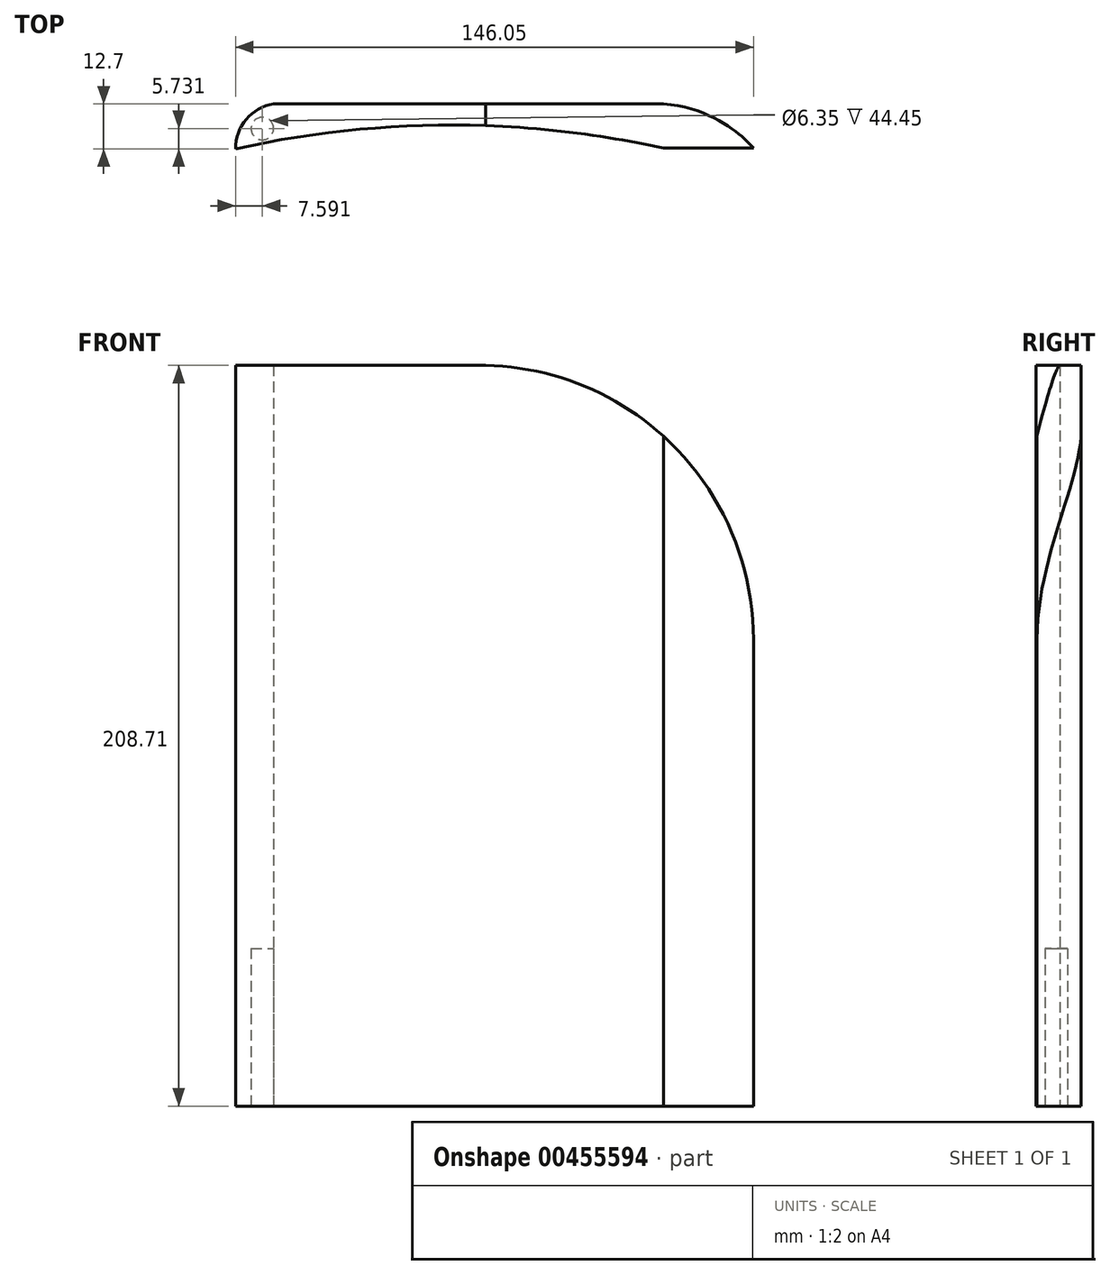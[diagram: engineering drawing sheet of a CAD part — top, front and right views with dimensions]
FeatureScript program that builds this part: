
annotation { "Feature Type Name" : "Feature", "Feature Type Description" : "" }
export const myFeature = defineFeature(function(context is Context, id is Id, definition is map)
    precondition{}
    {
        {
            var Q0;
            Q0=qCreatedBy(makeId("Front.planeOp"),FACE);
            var sketch = newSketch(context, id + "F0", { "sketchPlane" : qUnion([Q0])});
            skLineSegment(sketch, "E0", {"start": v(0, 0) * mm, "end": v(146.05, 0) * mm});
            skLineSegment(sketch, "E1", {"start": v(146.05, 0) * mm, "end": v(146.05, 131.57) * mm});
            skLineSegment(sketch, "E2", {"start": v(146.05, 131.57) * mm, "end": v(70.54, 208.71) * mm});
            skLineSegment(sketch, "E3", {"start": v(70.54, 208.71) * mm, "end": v(0, 127) * mm});
            skLineSegment(sketch, "E4", {"start": v(0, 127) * mm, "end": v(0, 0) * mm});
            skLineSegment(sketch, "E5", {"start": v(70.54, 208.71) * mm, "end": v(0, 208.71) * mm});
            skLineSegment(sketch, "E6", {"start": v(0, 208.71) * mm, "end": v(0, 127) * mm});
            skArc(sketch, "E7", {"start": v(146.05, 131.57) * mm, "mid": v(124.03, 185.54) * mm, "end": v(70.54, 208.71) * mm});
            skSolve(sketch);
        }
        {
            var Q0;
            Q0=qSketchRegion(id+"F0",true);
            extrude(context, id + "F1", {"entities" : qUnion([Q0]), "depth" : 12.7 * mm});
        }
        {
            var Q0;
            Q0=qCreatedBy(makeId("Top.planeOp"),FACE);
            var sketch = newSketch(context, id + "F2", { "sketchPlane" : qUnion([Q0])});
            skLineSegment(sketch, "E8", {"start": v(0, 0) * mm, "end": v(0, -12.7) * mm});
            skLineSegment(sketch, "E9", {"start": v(0, 0) * mm, "end": v(146.05, 0) * mm});
            skLineSegment(sketch, "E10", {"start": v(146.05, 0) * mm, "end": v(146.05, -12.42) * mm});
            skLineSegment(sketch, "E11", {"start": v(146.05, -12.42) * mm, "end": v(0, -12.7) * mm});
            skArc(sketch, "E12", {"start": v(120.65, -12.47) * mm, "mid": v(60.31, -6) * mm, "end": v(0, -12.7) * mm});
            skArc(sketch, "E13", {"start": v(15, 0) * mm, "mid": v(4.55, -2.88) * mm, "end": v(0, -12.7) * mm});
            skArc(sketch, "E14", {"start": v(146.05, -12.42) * mm, "mid": v(134.55, -3.77) * mm, "end": v(120.65, 0) * mm});
            skSolve(sketch);
        }
        {
            var Q0;
            {var subQ2=sQuery(id+"F2.wireOp",EDGE,"E12");Q0=makeQuery(id+"F2.imprint","IMPRINT",FACE,{"disambiguationData":[TD([[makeQuery(id+"F2.imprint","IMPRINT",EDGE,{"derivedFrom":subQ2}),-1.0]])]});}
            extrude(context, id + "F3", {"entities" : qUnion([Q0]), "operationType" : NewBodyOperationType.INTERSECT, "depth" : 2819.4 * mm});
        }
        {
            var Q0;
            Q0=makeQuery(id+"F1.opExtrude","SWEPT_FACE",FACE,{"disambiguationData":[OSD([sQuery(id+"F0.wireOp",EDGE,"E0")])]});
            var sketch = newSketch(context, id + "F4", { "sketchPlane" : qUnion([Q0])});
            skCircle(sketch, "E15", {"center": v(7.6, 6.97) * mm, "radius": 3.18 * mm});
            skSolve(sketch);
        }
        {
            var Q0;
            Q0 = qSketchRegion(id + "F4", true);
            extrude(context, id + "F5", {"entities" : qUnion([Q0]), "operationType" : NewBodyOperationType.REMOVE, "oppositeDirection" : true, "depth" : 44.45 * mm});
        }
    });
